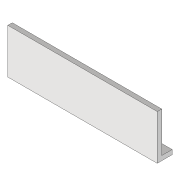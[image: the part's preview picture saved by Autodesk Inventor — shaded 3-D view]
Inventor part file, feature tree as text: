
AUTODESK INVENTOR PART (.ipt)
format: ipt  version: 2020 (Build 240168000, 168)  size: 78,336 bytes
history: native  units: mm
features: extrude x1, sketch x1
ambient origin geometry x8: Origin, YZ Plane, XZ Plane, XY Plane, X Axis, Y Axis, Z Axis, Center Point
bodies: Volumenkörper1 (feature_tree)
feature tree (2):
  extrude  "Extrusion1"  Depth=300.0mm
  sketch  "Skizze1"  dims[d0=100.0mm d1=300.0mm d2=30.0mm d3=30.0mm d4=1300.0mm d5=0.0mm]
